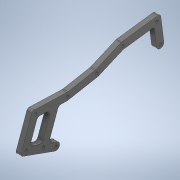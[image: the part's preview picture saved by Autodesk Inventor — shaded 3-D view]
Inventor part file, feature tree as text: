
AUTODESK INVENTOR PART (.ipt)
format: ipt  version: 2020 (Build 240168000, 168)  size: 308,224 bytes
history: native  units: in
note: dims shown in document units (in); Inventor stores cm internally (conversion verified against a paired STEP export)
features: sketch x4, projected_geometry x3, extrude x1
ambient origin geometry x8: Origin, YZ Plane, XZ Plane, XY Plane, X Axis, Y Axis, Z Axis, Center Point
bodies: Solid2 (feature_tree), Solid1 (feature_tree)
feature tree (8):
  extrude  "Extrusion1"  Depth=0.0787in
  sketch  "Sketch3"  dims[d3=0.122in]
  sketch  "Sketch4"  dims[d4=0.122in]
  sketch  "Sketch5"  dims[d5=0.122in d6=0.122in d7=0.122in d8=0.122in d9=0.122in d10=0.122in d11=10.4691in]
  sketch  "Sketch1"  dims[d0=0.0787in d1=0.0in d2=0.122in]
  projected_geometry  "Projected Loop1"
  projected_geometry  "Projected Loop2"
  projected_geometry  "Projected Loop3"
